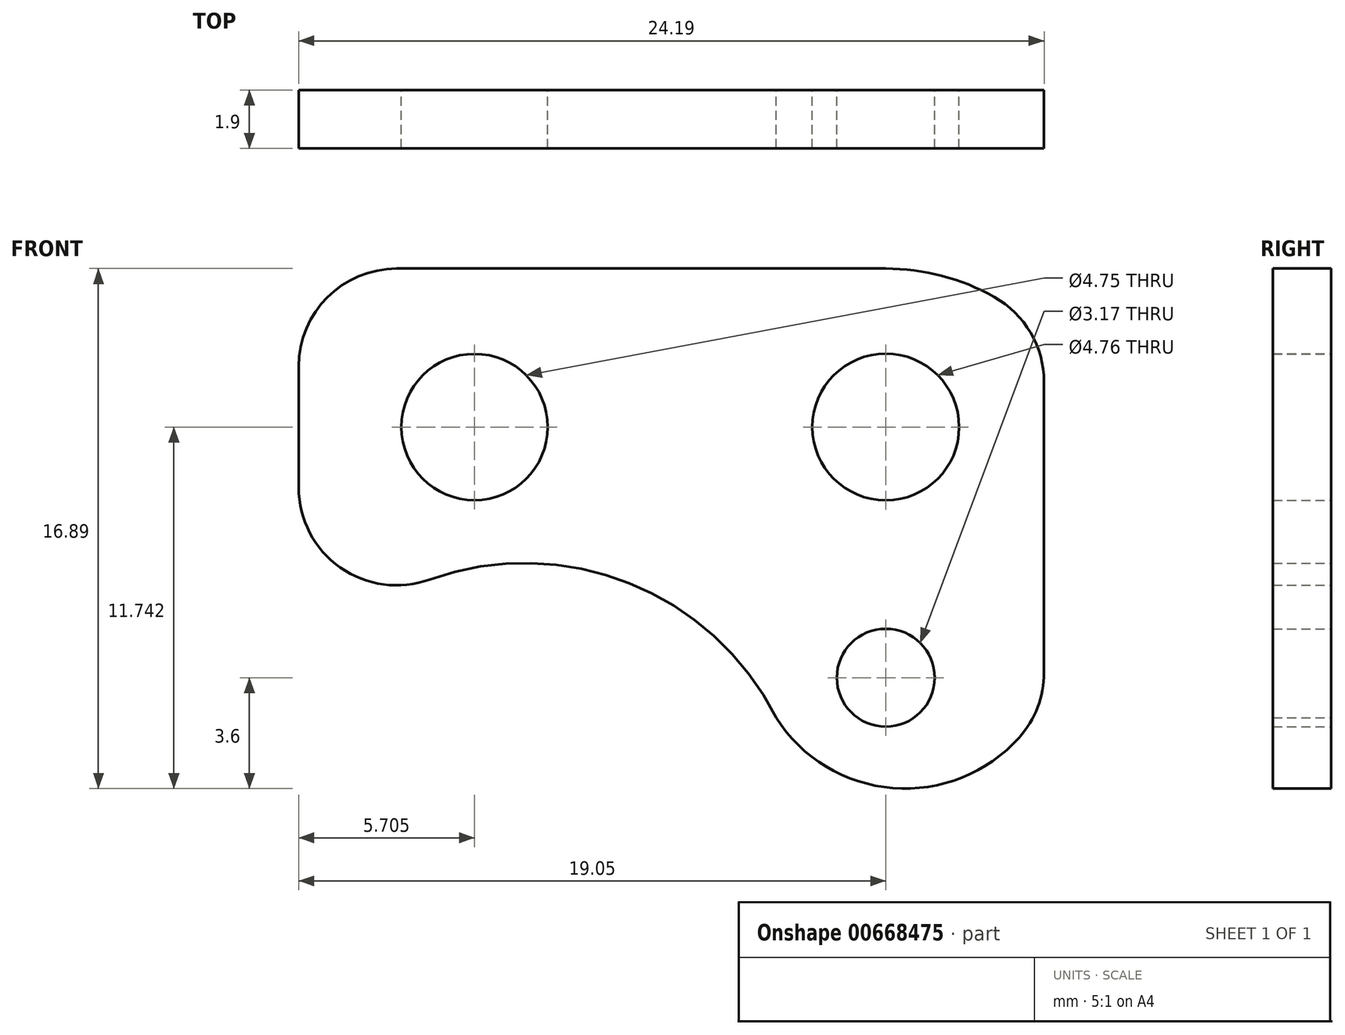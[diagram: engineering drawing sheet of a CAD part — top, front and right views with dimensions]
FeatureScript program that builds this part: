
annotation { "Feature Type Name" : "Feature", "Feature Type Description" : "" }
export const myFeature = defineFeature(function(context is Context, id is Id, definition is map)
    precondition{}
    {
        {
            var Q0;
            Q0=qCreatedBy(makeId("Front.planeOp"),FACE);
            var sketch = newSketch(context, id + "F0", { "sketchPlane" : qUnion([Q0])});
            skLineSegment(sketch, "E0", {"start": v(0, 13.29) * mm, "end": v(-15.88, 13.29) * mm});
            skArc(sketch, "E1", {"start": v(-3.56, -1.3) * mm, "mid": v(-8.33, 3.07) * mm, "end": v(-14.8, 3.19) * mm});
            skLineSegment(sketch, "E2", {"start": v(-19.05, 6.18) * mm, "end": v(-19.05, 10.11) * mm});
            skPoint(sketch, "E3.orphan", {"position": v(-31.69, 13.29) * mm});
            skPoint(sketch, "E4.orphan", {"position": v(-31.69, 0) * mm});
            skPoint(sketch, "E5.visualSharp", {"position": v(-19.05, 0.04) * mm});
            skArc(sketch, "E5.filletArc", {"start": v(-19.05, 6.18) * mm, "mid": v(-17.7, 3.58) * mm, "end": v(-14.8, 3.19) * mm});
            skPoint(sketch, "E6.visualSharp", {"position": v(-19.05, 13.29) * mm});
            skArc(sketch, "E6.filletArc", {"start": v(-15.88, 13.29) * mm, "mid": v(-18.12, 12.36) * mm, "end": v(-19.05, 10.11) * mm});
            skCircle(sketch, "E7", {"center": v(-13.35, 8.14) * mm, "radius": 2.37 * mm});
            skCircle(sketch, "E8", {"center": v(0, 0) * mm, "radius": 1.59 * mm});
            skCircle(sketch, "E9", {"center": v(0, 8.14) * mm, "radius": 2.38 * mm});
            skPoint(sketch, "E10.start.orphan", {"position": v(-19.05, 8.14) * mm});
            skArc(sketch, "E11", {"start": v(3.52, 12.37) * mm, "mid": v(1.82, 13.05) * mm, "end": v(0, 13.29) * mm});
            skPoint(sketch, "E12.orphan", {"position": v(3.79, 0) * mm});
            skArc(sketch, "E13", {"start": v(-3.56, -1.3) * mm, "mid": v(0.23, -3.58) * mm, "end": v(4.33, -1.94) * mm});
            skLineSegment(sketch, "E14", {"start": v(5.14, 0.17) * mm, "end": v(5.14, 9.6) * mm});
            skPoint(sketch, "E15.visualSharp", {"position": v(5.14, -0.71) * mm});
            skArc(sketch, "E15.filletArc", {"start": v(4.33, -1.94) * mm, "mid": v(4.93, -0.96) * mm, "end": v(5.14, 0.17) * mm});
            skPoint(sketch, "E16.visualSharp", {"position": v(5.14, 11.13) * mm});
            skArc(sketch, "E16.filletArc", {"start": v(5.14, 9.6) * mm, "mid": v(4.7, 11.2) * mm, "end": v(3.52, 12.37) * mm});
            skSolve(sketch);
        }
        {
            var Q0;
            Q0=makeQuery(id+"F0.imprint","IMPRINT",FACE,{"disambiguationData":[TD([[makeQuery(id+"F0.imprint","IMPRINT",EDGE,{"derivedFrom":sQuery(id+"F0.wireOp",EDGE,"E0")}),1.0]])]});
            extrude(context, id + "F1", {"entities" : qUnion([Q0]), "depth" : 1.9 * mm});
        }
    });
